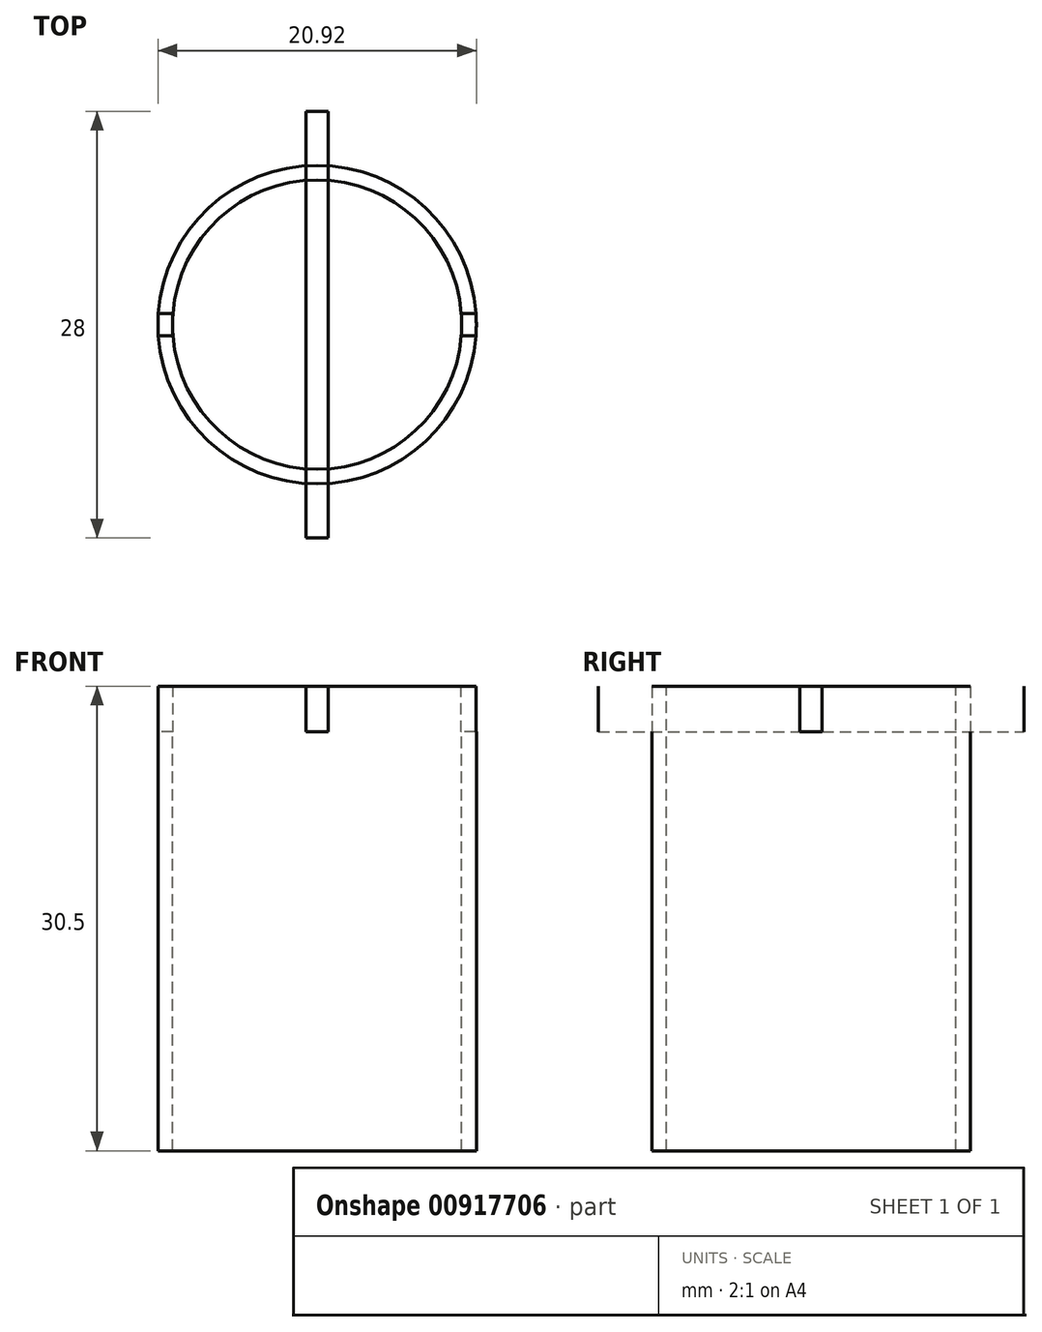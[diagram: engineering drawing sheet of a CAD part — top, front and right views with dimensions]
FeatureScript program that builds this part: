
annotation { "Feature Type Name" : "Feature", "Feature Type Description" : "" }
export const myFeature = defineFeature(function(context is Context, id is Id, definition is map)
    precondition{}
    {
        {
            assignVariable(context, id + "F0", {"name" : "height", "anyValue" : 30});
        }
        {
            assignVariable(context, id + "F1", {"name" : "slop", "anyValue" : .5});
        }
        {
            var Q0;
            Q0=qCreatedBy(makeId("Top.planeOp"),FACE);
            var sketch = newSketch(context, id + "F2", { "sketchPlane" : qUnion([Q0])});
            skCircle(sketch, "E0", {"center": v(0, 0) * mm, "radius": 10.46 * mm});
            skSolve(sketch);
        }
        {
            var Q0;
            Q0=makeQuery(id+"F2.imprint","IMPRINT",FACE,{"disambiguationData":[TD([[makeQuery(id+"F2.imprint","IMPRINT",EDGE,{"derivedFrom":sQuery(id+"F2.wireOp",EDGE,"E0")}),1.0]])]});
            extrude(context, id + "F3", {"entities" : qUnion([Q0]), "depth" : (getVariable(context, 'height') + getVariable(context, 'slop')) * mm, "offsetDistance" : 25 * mm});
        }
        {
            var Q0;
            Q0=makeQuery(id+"F3.opExtrude","CAP_FACE",FACE,{"disambiguationData":[OSD([sQuery(id+"F2.wireOp",EDGE,"E0")])],"isStart":false});
            var sketch = newSketch(context, id + "F4", { "sketchPlane" : qUnion([Q0])});
            skCircle(sketch, "E1", {"center": v(0, 0) * mm, "radius": 9.5 * mm});
            skSolve(sketch);
        }
        {
            var Q0;
            Q0=makeQuery(id+"F4.imprint","IMPRINT",FACE,{"disambiguationData":[TD([[makeQuery(id+"F4.imprint","IMPRINT",EDGE,{"derivedFrom":sQuery(id+"F4.wireOp",EDGE,"E1")}),1.0]])]});
            extrude(context, id + "F5", {"entities" : qUnion([Q0]), "operationType" : NewBodyOperationType.REMOVE, "endBound" : BoundingType.UP_TO_NEXT, "oppositeDirection" : true, "depth" : 25 * mm, "offsetDistance" : 25 * mm});
        }
        {
            var Q0;
            Q0=makeQuery(id+"F3.opExtrude","CAP_FACE",FACE,{"disambiguationData":[OSD([sQuery(id+"F2.wireOp",EDGE,"E0")])],"isStart":false});
            var sketch = newSketch(context, id + "F6", { "sketchPlane" : qUnion([Q0])});
            skLineSegment(sketch, "E2.bottom", {"start": v(14, 0.73) * mm, "end": v(-14, 0.73) * mm});
            skLineSegment(sketch, "E2.top", {"start": v(14, -0.73) * mm, "end": v(-14, -0.73) * mm});
            skLineSegment(sketch, "E2.left", {"start": v(14, 0.73) * mm, "end": v(14, -0.73) * mm});
            skLineSegment(sketch, "E2.right", {"start": v(-14, 0.73) * mm, "end": v(-14, -0.73) * mm});
            skPoint(sketch, "E2.middle", {"position": v(0, 0) * mm});
            skSolve(sketch);
        }
        {
            var Q0;
            Q0 = qSketchRegion(id + "F6", true);
            extrude(context, id + "F7", {"entities" : qUnion([Q0]), "oppositeDirection" : true, "depth" : 3 * mm, "offsetDistance" : 25 * mm});
        }
        {
            var Q0;
            Q0=makeQuery(id+"F7.opExtrude","SWEPT_BODY",BODY,{"disambiguationData":[OSD([sQuery(id+"F6.wireOp",EDGE,"E2.bottom"),sQuery(id+"F6.wireOp",EDGE,"E2.top"),sQuery(id+"F6.wireOp",EDGE,"E2.left"),sQuery(id+"F6.wireOp",EDGE,"E2.right")])]});
            var Q1;
            Q1=makeQuery(id+"F3.opExtrude","SWEPT_FACE",FACE,{"disambiguationData":[OSD([sQuery(id+"F2.wireOp",EDGE,"E0")])]});
            circularPattern(context, id + "F8", {"entities" : qUnion([Q0]), "axis" : qUnion([Q1]), "angle" : 90 * degree, "instanceCount" : 2, "equalSpace" : true});
        }
        {
            var Q0;
            Q0=makeQuery(id+"F7.opExtrude","SWEPT_BODY",BODY,{"disambiguationData":[OSD([sQuery(id+"F6.wireOp",EDGE,"E2.bottom"),sQuery(id+"F6.wireOp",EDGE,"E2.top"),sQuery(id+"F6.wireOp",EDGE,"E2.left"),sQuery(id+"F6.wireOp",EDGE,"E2.right")])]});
            var Q1;
            Q1=makeQuery(id+"F3.opExtrude","SWEPT_BODY",BODY,{"disambiguationData":[OSD([sQuery(id+"F2.wireOp",EDGE,"E0")])]});
            booleanBodies(context, id + "F9", {"operationType" : BooleanOperationType.SUBTRACTION, "tools" : qUnion([Q0]), "targets" : qUnion([Q1])});
        }
    });
